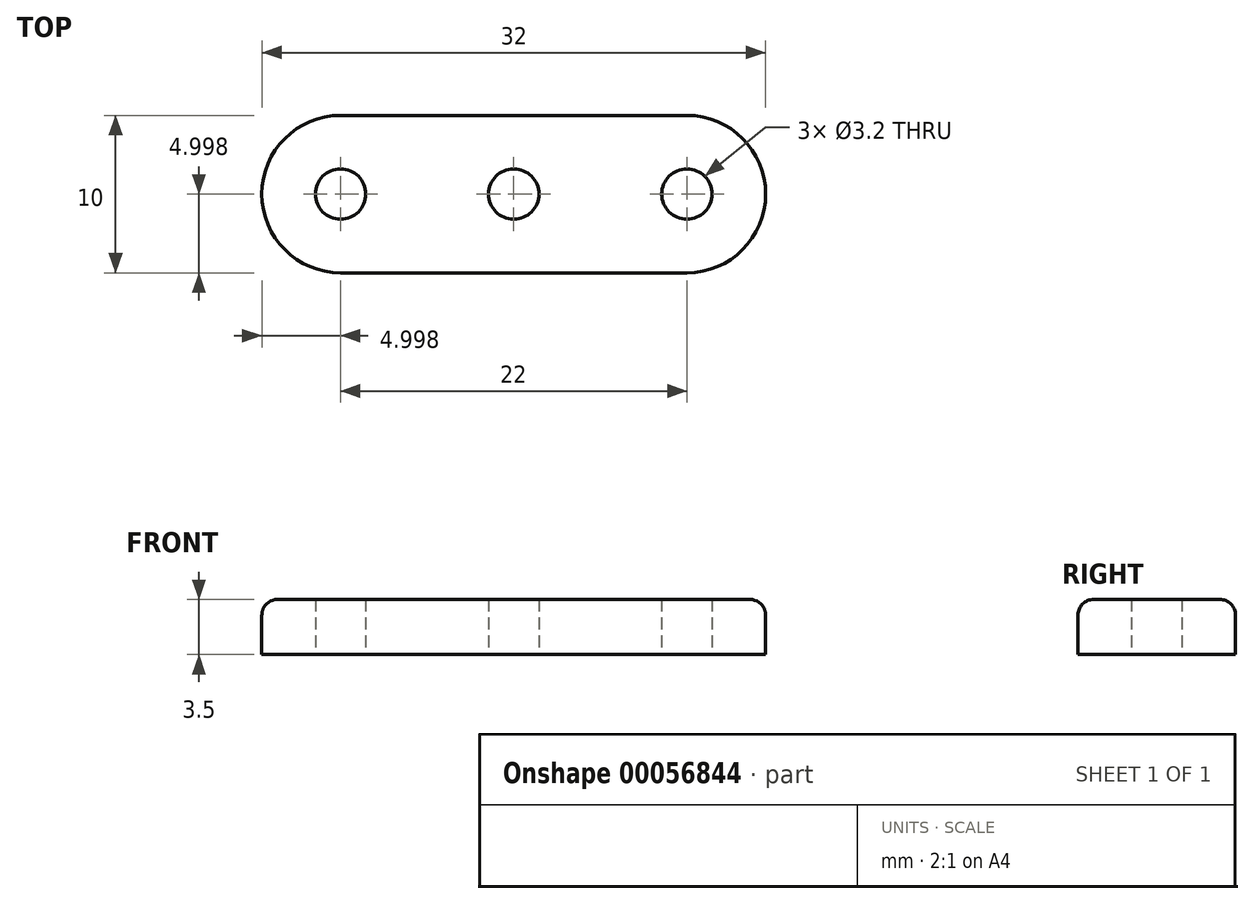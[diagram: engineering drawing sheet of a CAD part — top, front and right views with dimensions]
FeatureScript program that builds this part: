
annotation { "Feature Type Name" : "Feature", "Feature Type Description" : "" }
export const myFeature = defineFeature(function(context is Context, id is Id, definition is map)
    precondition{}
    {
        {
            var Q0;
            Q0=qCreatedBy(makeId("Top.planeOp"),FACE);
            var sketch = newSketch(context, id + "F0", { "sketchPlane" : qUnion([Q0])});
            skLineSegment(sketch, "E0.bottom", {"start": v(-25.42, 4.26) * mm, "end": v(6.58, 4.26) * mm});
            skLineSegment(sketch, "E0.top", {"start": v(-25.42, -5.74) * mm, "end": v(6.58, -5.74) * mm});
            skLineSegment(sketch, "E0.left", {"start": v(-25.42, 4.26) * mm, "end": v(-25.42, -5.74) * mm});
            skLineSegment(sketch, "E0.right", {"start": v(6.58, 4.26) * mm, "end": v(6.58, -5.74) * mm});
            skLineSegment(sketch, "E1.0", {"start": v(-27.42, -0.74) * mm, "end": v(8.58, -0.74) * mm, "construction": true});
            skLineSegment(sketch, "E2.0", {"start": v(-20.42, 4.26) * mm, "end": v(-20.42, -5.74) * mm, "construction": true});
            skLineSegment(sketch, "E3.0", {"start": v(-9.42, 4.26) * mm, "end": v(-9.42, -5.74) * mm, "construction": true});
            skLineSegment(sketch, "E4.0", {"start": v(1.58, 4.26) * mm, "end": v(1.58, -5.74) * mm, "construction": true});
            skCircle(sketch, "E5", {"center": v(-20.42, -0.74) * mm, "radius": 1.6 * mm});
            skCircle(sketch, "E6", {"center": v(-9.42, -0.74) * mm, "radius": 1.6 * mm});
            skCircle(sketch, "E7", {"center": v(1.58, -0.74) * mm, "radius": 1.6 * mm});
            skSolve(sketch);
        }
        {
            var Q0;
            Q0=makeQuery(id+"F0.imprint","IMPRINT",FACE,{"disambiguationData":[TD([[makeQuery(id+"F0.imprint","IMPRINT",EDGE,{"derivedFrom":sQuery(id+"F0.wireOp",EDGE,"E0.bottom")}),-1.0]])]});
            extrude(context, id + "F1", {"entities" : qUnion([Q0]), "depth" : 3.5 * mm});
        }
        {
            var Q0;
            Q0=makeQuery(id+"F1.opExtrude","SWEPT_EDGE",EDGE,{"disambiguationData":[OSD([sQuery(id+"F0.wireOp",EDGE,"E0.bottom"),sQuery(id+"F0.wireOp",EDGE,"E0.right")])]});
            var Q1;
            Q1=makeQuery(id+"F1.opExtrude","SWEPT_EDGE",EDGE,{"disambiguationData":[OSD([sQuery(id+"F0.wireOp",EDGE,"E0.top"),sQuery(id+"F0.wireOp",EDGE,"E0.right")])]});
            var Q2;
            Q2=makeQuery(id+"F1.opExtrude","SWEPT_EDGE",EDGE,{"disambiguationData":[OSD([sQuery(id+"F0.wireOp",EDGE,"E0.bottom"),sQuery(id+"F0.wireOp",EDGE,"E0.left")])]});
            var Q3;
            Q3=makeQuery(id+"F1.opExtrude","SWEPT_EDGE",EDGE,{"disambiguationData":[OSD([sQuery(id+"F0.wireOp",EDGE,"E0.top"),sQuery(id+"F0.wireOp",EDGE,"E0.left")])]});
            fillet(context, id + "F2", {"entities" : qUnion([Q0, Q1, Q2, Q3]), "radius" : 5 * mm, "tangentPropagation" : true, "allowEdgeOverflow" : false});
        }
        {
            var Q0;
            Q0=makeQuery(id+"F1.opExtrude","CAP_EDGE",EDGE,{"disambiguationData":[OSD([sQuery(id+"F0.wireOp",EDGE,"E0.bottom")])],"isStart":false});
            var Q1;
            Q1=makeQuery(id+"F1.opExtrude","CAP_EDGE",EDGE,{"disambiguationData":[OSD([sQuery(id+"F0.wireOp",EDGE,"E0.top")])],"isStart":false});
            fillet(context, id + "F3", {"entities" : qUnion([Q0, Q1]), "radius" : 1 * mm, "tangentPropagation" : true, "allowEdgeOverflow" : false});
        }
    });
